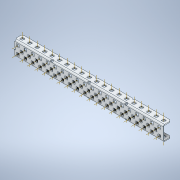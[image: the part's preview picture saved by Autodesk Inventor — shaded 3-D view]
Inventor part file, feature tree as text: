
AUTODESK INVENTOR PART (.ipt)
format: ipt  version: 2020 (Build 240168000, 168)  size: 1,346,560 bytes
history: native  units: in
note: dims shown in document units (in); Inventor stores cm internally (conversion verified against a paired STEP export)
features: other x103, plane x8, pattern_linear x4, split x3, sheet_metal_op x1
ambient origin geometry x8: Origin, YZ Plane, XZ Plane, XY Plane, X Axis, Y Axis, Z Axis, Center Point
bodies: Solid1 (feature_tree)
feature tree (119):
  other  "Work Axis1"
  pattern_linear  "Rectangular Pattern1"  Count1=20 Spacing1=0.5in
  other  "Work Axis72"
  pattern_linear  "Rectangular Pattern2"  Count1=20 Spacing1=0.5in
  pattern_linear  "Rectangular Pattern3"  Count1=20 Spacing1=0.5in
  other  "Work Axis141"
  pattern_linear  "Rectangular Pattern4"  Count1=19 Spacing1=0.5in
  plane  "Work Plane7"
  split  "Split1"
  plane  "Work Plane8"
  split  "Split2"
  split  "Split3"
  plane  "Work Plane1"
  plane  "Work Plane2"
  other  "Work Point1"
  other  "Work Axis2"
  other  "Work Axis3"
  other  "Work Axis4"
  other  "Work Axis5"
  other  "Work Axis6"
  other  "Work Axis7"
  other  "Work Axis8"
  other  "Work Axis9"
  other  "Work Axis10"
  other  "Work Axis11"
  other  "Work Axis12"
  other  "Work Axis13"
  other  "Work Axis14"
  other  "Work Axis15"
  other  "Work Axis16"
  other  "Work Axis17"
  other  "Work Axis18"
  other  "Work Axis19"
  other  "Work Axis20"
  other  "Work Axis36"
  other  "Work Axis37"
  other  "Work Axis38"
  other  "Work Axis39"
  other  "Work Axis40"
  other  "Work Axis41"
  other  "Work Axis42"
  other  "Work Axis43"
  other  "Work Axis44"
  other  "Work Axis45"
  other  "Work Axis46"
  other  "Work Axis47"
  other  "Work Axis48"
  other  "Work Axis49"
  other  "Work Axis50"
  other  "Work Axis51"
  other  "Work Axis52"
  other  "Work Axis53"
  other  "Work Axis54"
  other  "Work Axis55"
  plane  "Work Plane3"
  plane  "Work Plane4"
  other  "Work Point2"
  other  "Work Axis71"
  other  "Work Point3"
  other  "Work Axis73"
  other  "Work Axis74"
  other  "Work Axis75"
  other  "Work Axis76"
  other  "Work Axis77"
  other  "Work Axis78"
  other  "Work Axis79"
  other  "Work Axis80"
  other  "Work Axis81"
  other  "Work Axis82"
  other  "Work Axis83"
  other  "Work Axis84"
  other  "Work Axis85"
  other  "Work Axis86"
  other  "Work Axis87"
  other  "Work Axis88"
  other  "Work Axis89"
  other  "Work Axis90"
  other  "Work Axis91"
  other  "Work Axis107"
  other  "Work Axis108"
  other  "Work Axis109"
  other  "Work Axis110"
  other  "Work Axis111"
  other  "Work Axis112"
  other  "Work Axis113"
  other  "Work Axis114"
  other  "Work Axis115"
  other  "Work Axis116"
  other  "Work Axis117"
  other  "Work Axis118"
  other  "Work Axis119"
  other  "Work Axis120"
  other  "Work Axis121"
  other  "Work Axis122"
  other  "Work Axis123"
  other  "Work Axis124"
  other  "Work Axis125"
  plane  "Work Plane5"
  plane  "Work Plane6"
  other  "Work Point4"
  other  "Work Axis142"
  other  "Work Axis143"
  other  "Work Axis144"
  other  "Work Axis145"
  other  "Work Axis146"
  other  "Work Axis147"
  other  "Work Axis148"
  other  "Work Axis149"
  other  "Work Axis150"
  other  "Work Axis151"
  other  "Work Axis152"
  other  "Work Axis153"
  other  "Work Axis154"
  other  "Work Axis155"
  other  "Work Axis156"
  other  "Work Axis157"
  other  "Work Axis158"
  other  "Work Axis159"
  sheet_metal_op  "Fold1"
